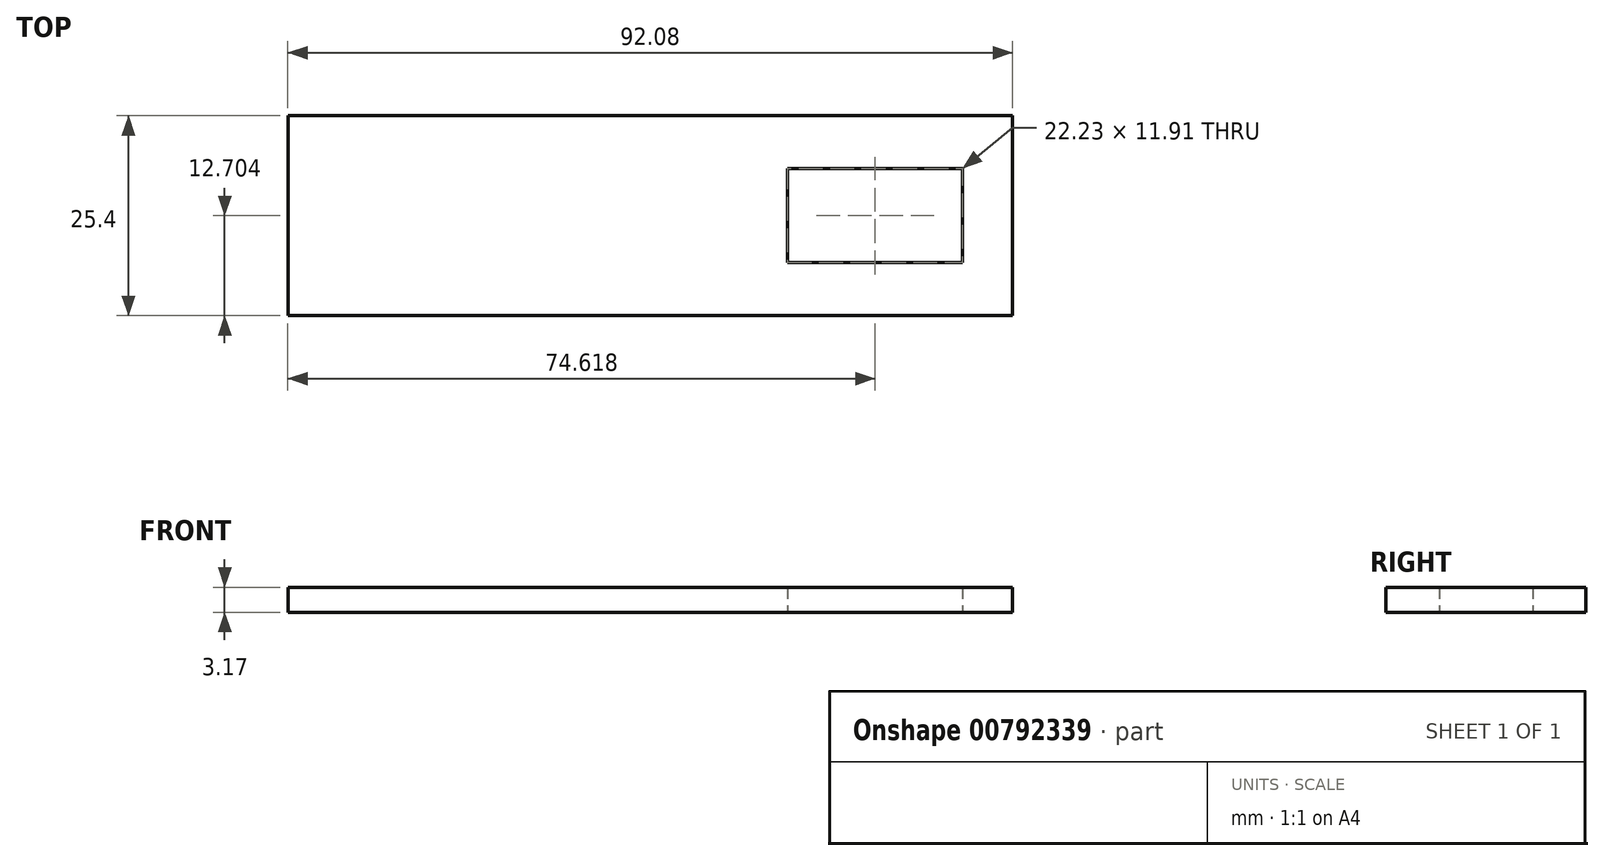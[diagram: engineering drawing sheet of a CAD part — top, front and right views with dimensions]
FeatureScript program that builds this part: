
annotation { "Feature Type Name" : "Feature", "Feature Type Description" : "" }
export const myFeature = defineFeature(function(context is Context, id is Id, definition is map)
    precondition{}
    {
        {
            var Q0;
            Q0=qCreatedBy(makeId("Top.planeOp"),FACE);
            var sketch = newSketch(context, id + "F0", { "sketchPlane" : qUnion([Q0])});
            skLineSegment(sketch, "E0.bottom", {"start": v(-92.07, 37.6) * mm, "end": v(0, 37.6) * mm});
            skLineSegment(sketch, "E0.top", {"start": v(-92.07, 12.2) * mm, "end": v(0, 12.2) * mm});
            skLineSegment(sketch, "E0.left", {"start": v(-92.07, 37.6) * mm, "end": v(-92.07, 12.2) * mm});
            skLineSegment(sketch, "E0.right", {"start": v(0, 37.6) * mm, "end": v(0, 12.2) * mm});
            skLineSegment(sketch, "E1.bottom", {"start": v(-28.57, 30.85) * mm, "end": v(-6.35, 30.85) * mm});
            skLineSegment(sketch, "E1.top", {"start": v(-28.57, 18.94) * mm, "end": v(-6.35, 18.94) * mm});
            skLineSegment(sketch, "E1.left", {"start": v(-28.57, 30.85) * mm, "end": v(-28.57, 18.94) * mm});
            skLineSegment(sketch, "E1.right", {"start": v(-6.35, 30.85) * mm, "end": v(-6.35, 18.94) * mm});
            skLineSegment(sketch, "E2", {"start": v(-17.46, 30.85) * mm, "end": v(-17.46, 37.6) * mm, "construction": true});
            skLineSegment(sketch, "E3", {"start": v(-17.46, 18.94) * mm, "end": v(-17.46, 12.2) * mm, "construction": true});
            skSolve(sketch);
        }
        {
            var Q0;
            Q0=makeQuery(id+"F0.imprint","IMPRINT",FACE,{"disambiguationData":[TD([[makeQuery(id+"F0.imprint","IMPRINT",EDGE,{"derivedFrom":sQuery(id+"F0.wireOp",EDGE,"E0.bottom")}),-1.0]])]});
            extrude(context, id + "F1", {"entities" : qUnion([Q0]), "depth" : 3.17 * mm, "offsetDistance" : 25.4 * mm});
        }
    });
